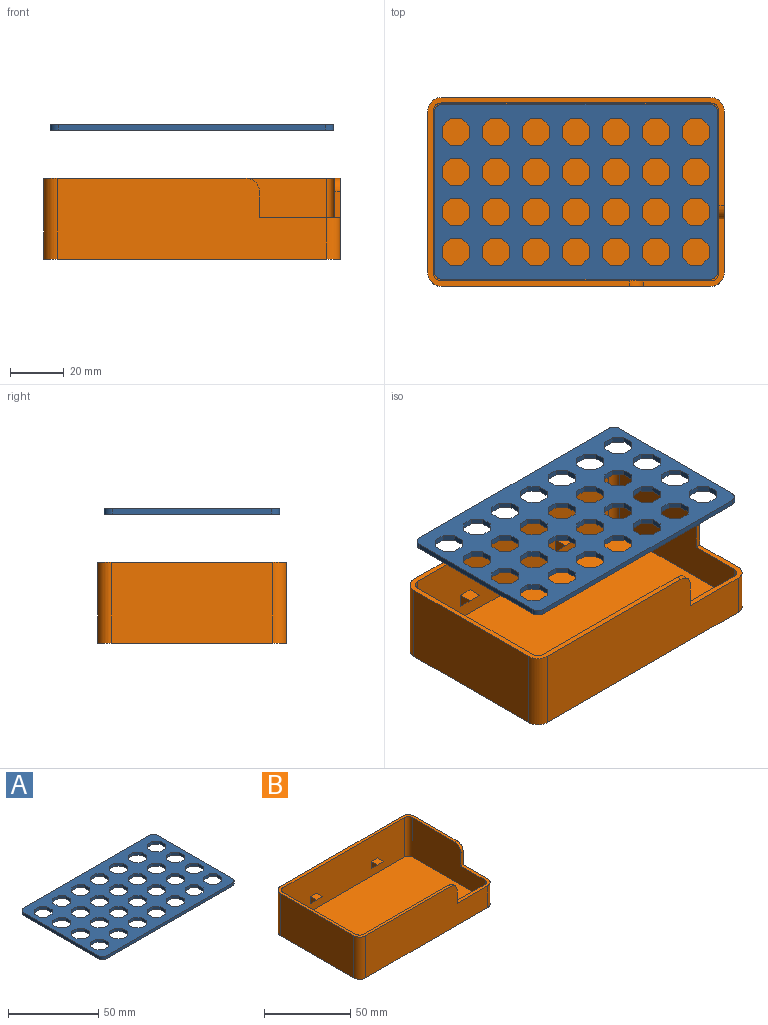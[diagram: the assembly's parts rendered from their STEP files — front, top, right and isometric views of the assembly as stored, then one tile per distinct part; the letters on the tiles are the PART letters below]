
ASSEMBLY  parts=2 mates=1
PART A: 234 faces, bbox 105x65x2 mm
  f0: plane 59x2mm, normal (1,0,0), area 118mm2, adj f1,f231,f232,f233
  f1: cylinder r=3mm len=3mm, axis (0,0,-1), area 9.4mm2, adj f0,f2,f232,f233
  f2: plane 99x2mm, normal (0,1,0), area 198mm2, adj f1,f3,f232,f233
  f3: cylinder r=3mm len=3mm, axis (0,0,-1), area 9.4mm2, adj f2,f4,f232,f233
  f4: plane 59x2mm, normal (-1,0,0), area 118mm2, adj f3,f5,f232,f233
  f5: cylinder r=3mm len=3mm, axis (0,0,-1), area 9.4mm2, adj f4,f6,f232,f233
  f6: plane 99x2mm, normal (0,-1,0), area 198mm2, adj f5,f231,f232,f233
  f7: plane 4.14x2mm, normal (0,-1,0), area 8.3mm2, adj f8,f203,f232,f233
  f8: plane 2.93x2.93mm, normal (-0.71,-0.71,0), area 8.3mm2, adj f7,f9,f232,f233
  f9: plane 4.14x2mm, normal (-1,0,0), area 8.3mm2, adj f8,f10,f232,f233
  f10: plane 2.93x2.93mm, normal (-0.71,0.71,0), area 8.3mm2, adj f9,f11,f232,f233
  f11: plane 4.14x2mm, normal (0,1,0), area 8.3mm2, adj f10,f12,f232,f233
  f12: plane 2.93x2.93mm, normal (0.71,0.71,0), area 8.3mm2, adj f11,f13,f232,f233
  f13: plane 4.14x2mm, normal (1,0,0), area 8.3mm2, adj f12,f203,f232,f233
  f14: plane 4.14x2mm, normal (-1,0,0), area 8.3mm2, adj f15,f204,f232,f233
  f15: plane 2.93x2.93mm, normal (-0.71,0.71,0), area 8.3mm2, adj f14,f16,f232,f233
  f16: plane 4.14x2mm, normal (0,1,0), area 8.3mm2, adj f15,f17,f232,f233
  f17: plane 2.93x2.93mm, normal (0.71,0.71,0), area 8.3mm2, adj f16,f18,f232,f233
  f18: plane 4.14x2mm, normal (1,0,0), area 8.3mm2, adj f17,f19,f232,f233
  f19: plane 2.93x2.93mm, normal (0.71,-0.71,0), area 8.3mm2, adj f18,f20,f232,f233
  f20: plane 4.14x2mm, normal (0,-1,0), area 8.3mm2, adj f19,f204,f232,f233
  f21: plane 4.14x2mm, normal (-1,0,0), area 8.3mm2, adj f22,f205,f232,f233
  f22: plane 2.93x2.93mm, normal (-0.71,0.71,0), area 8.3mm2, adj f21,f23,f232,f233
  f23: plane 4.14x2mm, normal (0,1,0), area 8.3mm2, adj f22,f24,f232,f233
  f24: plane 2.93x2.93mm, normal (0.71,0.71,0), area 8.3mm2, adj f23,f25,f232,f233
  f25: plane 4.14x2mm, normal (1,0,0), area 8.3mm2, adj f24,f26,f232,f233
  f26: plane 2.93x2.93mm, normal (0.71,-0.71,0), area 8.3mm2, adj f25,f27,f232,f233
  f27: plane 4.14x2mm, normal (0,-1,0), area 8.3mm2, adj f26,f205,f232,f233
  f28: plane 4.14x2mm, normal (-1,0,0), area 8.3mm2, adj f29,f206,f232,f233
  f29: plane 2.93x2.93mm, normal (-0.71,0.71,0), area 8.3mm2, adj f28,f30,f232,f233
  f30: plane 4.14x2mm, normal (0,1,0), area 8.3mm2, adj f29,f31,f232,f233
  f31: plane 2.93x2.93mm, normal (0.71,0.71,0), area 8.3mm2, adj f30,f32,f232,f233
  f32: plane 4.14x2mm, normal (1,0,0), area 8.3mm2, adj f31,f33,f232,f233
  f33: plane 2.93x2.93mm, normal (0.71,-0.71,0), area 8.3mm2, adj f32,f34,f232,f233
  f34: plane 4.14x2mm, normal (0,-1,0), area 8.3mm2, adj f33,f206,f232,f233
  f35: plane 4.14x2mm, normal (-1,0,0), area 8.3mm2, adj f36,f207,f232,f233
  f36: plane 2.93x2.93mm, normal (-0.71,0.71,0), area 8.3mm2, adj f35,f37,f232,f233
  f37: plane 4.14x2mm, normal (0,1,0), area 8.3mm2, adj f36,f38,f232,f233
  f38: plane 2.93x2.93mm, normal (0.71,0.71,0), area 8.3mm2, adj f37,f39,f232,f233
  f39: plane 4.14x2mm, normal (1,0,0), area 8.3mm2, adj f38,f40,f232,f233
  f40: plane 2.93x2.93mm, normal (0.71,-0.71,0), area 8.3mm2, adj f39,f41,f232,f233
  f41: plane 4.14x2mm, normal (0,-1,0), area 8.3mm2, adj f40,f207,f232,f233
  f42: plane 4.14x2mm, normal (-1,0,0), area 8.3mm2, adj f43,f208,f232,f233
  f43: plane 2.93x2.93mm, normal (-0.71,0.71,0), area 8.3mm2, adj f42,f44,f232,f233
  f44: plane 4.14x2mm, normal (0,1,0), area 8.3mm2, adj f43,f45,f232,f233
  f45: plane 2.93x2.93mm, normal (0.71,0.71,0), area 8.3mm2, adj f44,f46,f232,f233
  f46: plane 4.14x2mm, normal (1,0,0), area 8.3mm2, adj f45,f47,f232,f233
  f47: plane 2.93x2.93mm, normal (0.71,-0.71,0), area 8.3mm2, adj f46,f48,f232,f233
  f48: plane 4.14x2mm, normal (0,-1,0), area 8.3mm2, adj f47,f208,f232,f233
  f49: plane 4.14x2mm, normal (-1,0,0), area 8.3mm2, adj f50,f209,f232,f233
  f50: plane 2.93x2.93mm, normal (-0.71,0.71,0), area 8.3mm2, adj f49,f51,f232,f233
  f51: plane 4.14x2mm, normal (0,1,0), area 8.3mm2, adj f50,f52,f232,f233
  f52: plane 2.93x2.93mm, normal (0.71,0.71,0), area 8.3mm2, adj f51,f53,f232,f233
  f53: plane 4.14x2mm, normal (1,0,0), area 8.3mm2, adj f52,f54,f232,f233
  f54: plane 2.93x2.93mm, normal (0.71,-0.71,0), area 8.3mm2, adj f53,f55,f232,f233
  f55: plane 4.14x2mm, normal (0,-1,0), area 8.3mm2, adj f54,f209,f232,f233
  f56: plane 4.14x2mm, normal (-1,0,0), area 8.3mm2, adj f57,f210,f232,f233
  f57: plane 2.93x2.93mm, normal (-0.71,0.71,0), area 8.3mm2, adj f56,f58,f232,f233
  f58: plane 4.14x2mm, normal (0,1,0), area 8.3mm2, adj f57,f59,f232,f233
  f59: plane 2.93x2.93mm, normal (0.71,0.71,0), area 8.3mm2, adj f58,f60,f232,f233
  f60: plane 4.14x2mm, normal (1,0,0), area 8.3mm2, adj f59,f61,f232,f233
  f61: plane 2.93x2.93mm, normal (0.71,-0.71,0), area 8.3mm2, adj f60,f62,f232,f233
  f62: plane 4.14x2mm, normal (0,-1,0), area 8.3mm2, adj f61,f210,f232,f233
  f63: plane 4.14x2mm, normal (-1,0,0), area 8.3mm2, adj f64,f211,f232,f233
  f64: plane 2.93x2.93mm, normal (-0.71,0.71,0), area 8.3mm2, adj f63,f65,f232,f233
  f65: plane 4.14x2mm, normal (0,1,0), area 8.3mm2, adj f64,f66,f232,f233
  f66: plane 2.93x2.93mm, normal (0.71,0.71,0), area 8.3mm2, adj f65,f67,f232,f233
  f67: plane 4.14x2mm, normal (1,0,0), area 8.3mm2, adj f66,f68,f232,f233
  f68: plane 2.93x2.93mm, normal (0.71,-0.71,0), area 8.3mm2, adj f67,f69,f232,f233
  f69: plane 4.14x2mm, normal (0,-1,0), area 8.3mm2, adj f68,f211,f232,f233
  f70: plane 4.14x2mm, normal (-1,0,0), area 8.3mm2, adj f71,f212,f232,f233
  f71: plane 2.93x2.93mm, normal (-0.71,0.71,0), area 8.3mm2, adj f70,f72,f232,f233
  f72: plane 4.14x2mm, normal (0,1,0), area 8.3mm2, adj f71,f73,f232,f233
  f73: plane 2.93x2.93mm, normal (0.71,0.71,0), area 8.3mm2, adj f72,f74,f232,f233
  f74: plane 4.14x2mm, normal (1,0,0), area 8.3mm2, adj f73,f75,f232,f233
  f75: plane 2.93x2.93mm, normal (0.71,-0.71,0), area 8.3mm2, adj f74,f76,f232,f233
  f76: plane 4.14x2mm, normal (0,-1,0), area 8.3mm2, adj f75,f212,f232,f233
  f77: plane 4.14x2mm, normal (-1,0,0), area 8.3mm2, adj f78,f213,f232,f233
  f78: plane 2.93x2.93mm, normal (-0.71,0.71,0), area 8.3mm2, adj f77,f79,f232,f233
  f79: plane 4.14x2mm, normal (0,1,0), area 8.3mm2, adj f78,f80,f232,f233
  f80: plane 2.93x2.93mm, normal (0.71,0.71,0), area 8.3mm2, adj f79,f81,f232,f233
  f81: plane 4.14x2mm, normal (1,0,0), area 8.3mm2, adj f80,f82,f232,f233
  f82: plane 2.93x2.93mm, normal (0.71,-0.71,0), area 8.3mm2, adj f81,f83,f232,f233
  f83: plane 4.14x2mm, normal (0,-1,0), area 8.3mm2, adj f82,f213,f232,f233
  f84: plane 4.14x2mm, normal (-1,0,0), area 8.3mm2, adj f85,f214,f232,f233
  f85: plane 2.93x2.93mm, normal (-0.71,0.71,0), area 8.3mm2, adj f84,f86,f232,f233
  f86: plane 4.14x2mm, normal (0,1,0), area 8.3mm2, adj f85,f87,f232,f233
  f87: plane 2.93x2.93mm, normal (0.71,0.71,0), area 8.3mm2, adj f86,f88,f232,f233
  f88: plane 4.14x2mm, normal (1,0,0), area 8.3mm2, adj f87,f89,f232,f233
  f89: plane 2.93x2.93mm, normal (0.71,-0.71,0), area 8.3mm2, adj f88,f90,f232,f233
  f90: plane 4.14x2mm, normal (0,-1,0), area 8.3mm2, adj f89,f214,f232,f233
  f91: plane 4.14x2mm, normal (-1,0,0), area 8.3mm2, adj f92,f215,f232,f233
  f92: plane 2.93x2.93mm, normal (-0.71,0.71,0), area 8.3mm2, adj f91,f93,f232,f233
  f93: plane 4.14x2mm, normal (0,1,0), area 8.3mm2, adj f92,f94,f232,f233
  f94: plane 2.93x2.93mm, normal (0.71,0.71,0), area 8.3mm2, adj f93,f95,f232,f233
  f95: plane 4.14x2mm, normal (1,0,0), area 8.3mm2, adj f94,f96,f232,f233
  f96: plane 2.93x2.93mm, normal (0.71,-0.71,0), area 8.3mm2, adj f95,f97,f232,f233
  f97: plane 4.14x2mm, normal (0,-1,0), area 8.3mm2, adj f96,f215,f232,f233
  f98: plane 4.14x2mm, normal (-1,0,0), area 8.3mm2, adj f99,f216,f232,f233
  f99: plane 2.93x2.93mm, normal (-0.71,0.71,0), area 8.3mm2, adj f98,f100,f232,f233
  f100: plane 4.14x2mm, normal (0,1,0), area 8.3mm2, adj f99,f101,f232,f233
  f101: plane 2.93x2.93mm, normal (0.71,0.71,0), area 8.3mm2, adj f100,f102,f232,f233
  f102: plane 4.14x2mm, normal (1,0,0), area 8.3mm2, adj f101,f103,f232,f233
  f103: plane 2.93x2.93mm, normal (0.71,-0.71,0), area 8.3mm2, adj f102,f104,f232,f233
  f104: plane 4.14x2mm, normal (0,-1,0), area 8.3mm2, adj f103,f216,f232,f233
  f105: plane 4.14x2mm, normal (-1,0,0), area 8.3mm2, adj f106,f217,f232,f233
  f106: plane 2.93x2.93mm, normal (-0.71,0.71,0), area 8.3mm2, adj f105,f107,f232,f233
  f107: plane 4.14x2mm, normal (0,1,0), area 8.3mm2, adj f106,f108,f232,f233
  f108: plane 2.93x2.93mm, normal (0.71,0.71,0), area 8.3mm2, adj f107,f109,f232,f233
  f109: plane 4.14x2mm, normal (1,0,0), area 8.3mm2, adj f108,f110,f232,f233
  f110: plane 2.93x2.93mm, normal (0.71,-0.71,0), area 8.3mm2, adj f109,f111,f232,f233
  f111: plane 4.14x2mm, normal (0,-1,0), area 8.3mm2, adj f110,f217,f232,f233
  f112: plane 4.14x2mm, normal (-1,0,0), area 8.3mm2, adj f113,f218,f232,f233
  f113: plane 2.93x2.93mm, normal (-0.71,0.71,0), area 8.3mm2, adj f112,f114,f232,f233
  f114: plane 4.14x2mm, normal (0,1,0), area 8.3mm2, adj f113,f115,f232,f233
  f115: plane 2.93x2.93mm, normal (0.71,0.71,0), area 8.3mm2, adj f114,f116,f232,f233
  f116: plane 4.14x2mm, normal (1,0,0), area 8.3mm2, adj f115,f117,f232,f233
  f117: plane 2.93x2.93mm, normal (0.71,-0.71,0), area 8.3mm2, adj f116,f118,f232,f233
  f118: plane 4.14x2mm, normal (0,-1,0), area 8.3mm2, adj f117,f218,f232,f233
  f119: plane 4.14x2mm, normal (-1,0,0), area 8.3mm2, adj f120,f219,f232,f233
  f120: plane 2.93x2.93mm, normal (-0.71,0.71,0), area 8.3mm2, adj f119,f121,f232,f233
  f121: plane 4.14x2mm, normal (0,1,0), area 8.3mm2, adj f120,f122,f232,f233
  f122: plane 2.93x2.93mm, normal (0.71,0.71,0), area 8.3mm2, adj f121,f123,f232,f233
  f123: plane 4.14x2mm, normal (1,0,0), area 8.3mm2, adj f122,f124,f232,f233
  f124: plane 2.93x2.93mm, normal (0.71,-0.71,0), area 8.3mm2, adj f123,f125,f232,f233
  f125: plane 4.14x2mm, normal (0,-1,0), area 8.3mm2, adj f124,f219,f232,f233
  f126: plane 4.14x2mm, normal (-1,0,0), area 8.3mm2, adj f127,f220,f232,f233
  f127: plane 2.93x2.93mm, normal (-0.71,0.71,0), area 8.3mm2, adj f126,f128,f232,f233
  f128: plane 4.14x2mm, normal (0,1,0), area 8.3mm2, adj f127,f129,f232,f233
  f129: plane 2.93x2.93mm, normal (0.71,0.71,0), area 8.3mm2, adj f128,f130,f232,f233
  f130: plane 4.14x2mm, normal (1,0,0), area 8.3mm2, adj f129,f131,f232,f233
  f131: plane 2.93x2.93mm, normal (0.71,-0.71,0), area 8.3mm2, adj f130,f132,f232,f233
  f132: plane 4.14x2mm, normal (0,-1,0), area 8.3mm2, adj f131,f220,f232,f233
  f133: plane 4.14x2mm, normal (-1,0,0), area 8.3mm2, adj f134,f221,f232,f233
  f134: plane 2.93x2.93mm, normal (-0.71,0.71,0), area 8.3mm2, adj f133,f135,f232,f233
  f135: plane 4.14x2mm, normal (0,1,0), area 8.3mm2, adj f134,f136,f232,f233
  f136: plane 2.93x2.93mm, normal (0.71,0.71,0), area 8.3mm2, adj f135,f137,f232,f233
  f137: plane 4.14x2mm, normal (1,0,0), area 8.3mm2, adj f136,f138,f232,f233
  f138: plane 2.93x2.93mm, normal (0.71,-0.71,0), area 8.3mm2, adj f137,f139,f232,f233
  f139: plane 4.14x2mm, normal (0,-1,0), area 8.3mm2, adj f138,f221,f232,f233
  f140: plane 4.14x2mm, normal (-1,0,0), area 8.3mm2, adj f141,f222,f232,f233
  f141: plane 2.93x2.93mm, normal (-0.71,0.71,0), area 8.3mm2, adj f140,f142,f232,f233
  f142: plane 4.14x2mm, normal (0,1,0), area 8.3mm2, adj f141,f143,f232,f233
  f143: plane 2.93x2.93mm, normal (0.71,0.71,0), area 8.3mm2, adj f142,f144,f232,f233
  f144: plane 4.14x2mm, normal (1,0,0), area 8.3mm2, adj f143,f145,f232,f233
  f145: plane 2.93x2.93mm, normal (0.71,-0.71,0), area 8.3mm2, adj f144,f146,f232,f233
  f146: plane 4.14x2mm, normal (0,-1,0), area 8.3mm2, adj f145,f222,f232,f233
  f147: plane 4.14x2mm, normal (-1,0,0), area 8.3mm2, adj f148,f223,f232,f233
  f148: plane 2.93x2.93mm, normal (-0.71,0.71,0), area 8.3mm2, adj f147,f149,f232,f233
  f149: plane 4.14x2mm, normal (0,1,0), area 8.3mm2, adj f148,f150,f232,f233
  f150: plane 2.93x2.93mm, normal (0.71,0.71,0), area 8.3mm2, adj f149,f151,f232,f233
  f151: plane 4.14x2mm, normal (1,0,0), area 8.3mm2, adj f150,f152,f232,f233
  f152: plane 2.93x2.93mm, normal (0.71,-0.71,0), area 8.3mm2, adj f151,f153,f232,f233
  f153: plane 4.14x2mm, normal (0,-1,0), area 8.3mm2, adj f152,f223,f232,f233
  f154: plane 4.14x2mm, normal (-1,0,0), area 8.3mm2, adj f155,f224,f232,f233
  f155: plane 2.93x2.93mm, normal (-0.71,0.71,0), area 8.3mm2, adj f154,f156,f232,f233
  f156: plane 4.14x2mm, normal (0,1,0), area 8.3mm2, adj f155,f157,f232,f233
  f157: plane 2.93x2.93mm, normal (0.71,0.71,0), area 8.3mm2, adj f156,f158,f232,f233
  f158: plane 4.14x2mm, normal (1,0,0), area 8.3mm2, adj f157,f159,f232,f233
  f159: plane 2.93x2.93mm, normal (0.71,-0.71,0), area 8.3mm2, adj f158,f160,f232,f233
  f160: plane 4.14x2mm, normal (0,-1,0), area 8.3mm2, adj f159,f224,f232,f233
  f161: plane 4.14x2mm, normal (-1,0,0), area 8.3mm2, adj f162,f225,f232,f233
  f162: plane 2.93x2.93mm, normal (-0.71,0.71,0), area 8.3mm2, adj f161,f163,f232,f233
  f163: plane 4.14x2mm, normal (0,1,0), area 8.3mm2, adj f162,f164,f232,f233
  f164: plane 2.93x2.93mm, normal (0.71,0.71,0), area 8.3mm2, adj f163,f165,f232,f233
  f165: plane 4.14x2mm, normal (1,0,0), area 8.3mm2, adj f164,f166,f232,f233
  f166: plane 2.93x2.93mm, normal (0.71,-0.71,0), area 8.3mm2, adj f165,f167,f232,f233
  f167: plane 4.14x2mm, normal (0,-1,0), area 8.3mm2, adj f166,f225,f232,f233
  f168: plane 4.14x2mm, normal (-1,0,0), area 8.3mm2, adj f169,f226,f232,f233
  f169: plane 2.93x2.93mm, normal (-0.71,0.71,0), area 8.3mm2, adj f168,f170,f232,f233
  f170: plane 4.14x2mm, normal (0,1,0), area 8.3mm2, adj f169,f171,f232,f233
  f171: plane 2.93x2.93mm, normal (0.71,0.71,0), area 8.3mm2, adj f170,f172,f232,f233
  f172: plane 4.14x2mm, normal (1,0,0), area 8.3mm2, adj f171,f173,f232,f233
  f173: plane 2.93x2.93mm, normal (0.71,-0.71,0), area 8.3mm2, adj f172,f174,f232,f233
  f174: plane 4.14x2mm, normal (0,-1,0), area 8.3mm2, adj f173,f226,f232,f233
  f175: plane 4.14x2mm, normal (-1,0,0), area 8.3mm2, adj f176,f227,f232,f233
  f176: plane 2.93x2.93mm, normal (-0.71,0.71,0), area 8.3mm2, adj f175,f177,f232,f233
  f177: plane 4.14x2mm, normal (0,1,0), area 8.3mm2, adj f176,f178,f232,f233
  f178: plane 2.93x2.93mm, normal (0.71,0.71,0), area 8.3mm2, adj f177,f179,f232,f233
  f179: plane 4.14x2mm, normal (1,0,0), area 8.3mm2, adj f178,f180,f232,f233
  f180: plane 2.93x2.93mm, normal (0.71,-0.71,0), area 8.3mm2, adj f179,f181,f232,f233
  f181: plane 4.14x2mm, normal (0,-1,0), area 8.3mm2, adj f180,f227,f232,f233
  f182: plane 4.14x2mm, normal (-1,0,0), area 8.3mm2, adj f183,f228,f232,f233
  f183: plane 2.93x2.93mm, normal (-0.71,0.71,0), area 8.3mm2, adj f182,f184,f232,f233
  f184: plane 4.14x2mm, normal (0,1,0), area 8.3mm2, adj f183,f185,f232,f233
  f185: plane 2.93x2.93mm, normal (0.71,0.71,0), area 8.3mm2, adj f184,f186,f232,f233
  f186: plane 4.14x2mm, normal (1,0,0), area 8.3mm2, adj f185,f187,f232,f233
  f187: plane 2.93x2.93mm, normal (0.71,-0.71,0), area 8.3mm2, adj f186,f188,f232,f233
  f188: plane 4.14x2mm, normal (0,-1,0), area 8.3mm2, adj f187,f228,f232,f233
  f189: plane 4.14x2mm, normal (-1,0,0), area 8.3mm2, adj f190,f229,f232,f233
  f190: plane 2.93x2.93mm, normal (-0.71,0.71,0), area 8.3mm2, adj f189,f191,f232,f233
  f191: plane 4.14x2mm, normal (0,1,0), area 8.3mm2, adj f190,f192,f232,f233
  f192: plane 2.93x2.93mm, normal (0.71,0.71,0), area 8.3mm2, adj f191,f193,f232,f233
  f193: plane 4.14x2mm, normal (1,0,0), area 8.3mm2, adj f192,f194,f232,f233
  f194: plane 2.93x2.93mm, normal (0.71,-0.71,0), area 8.3mm2, adj f193,f195,f232,f233
  f195: plane 4.14x2mm, normal (0,-1,0), area 8.3mm2, adj f194,f229,f232,f233
  f196: plane 4.14x2mm, normal (-1,0,0), area 8.3mm2, adj f197,f230,f232,f233
  f197: plane 2.93x2.93mm, normal (-0.71,0.71,0), area 8.3mm2, adj f196,f198,f232,f233
  f198: plane 4.14x2mm, normal (0,1,0), area 8.3mm2, adj f197,f199,f232,f233
  f199: plane 2.93x2.93mm, normal (0.71,0.71,0), area 8.3mm2, adj f198,f200,f232,f233
  f200: plane 4.14x2mm, normal (1,0,0), area 8.3mm2, adj f199,f201,f232,f233
  f201: plane 2.93x2.93mm, normal (0.71,-0.71,0), area 8.3mm2, adj f200,f202,f232,f233
  f202: plane 4.14x2mm, normal (0,-1,0), area 8.3mm2, adj f201,f230,f232,f233
  f203: plane 2.93x2.93mm, normal (0.71,-0.71,0), area 8.3mm2, adj f7,f13,f232,f233
  f204: plane 2.93x2.93mm, normal (-0.71,-0.71,0), area 8.3mm2, adj f14,f20,f232,f233
  f205: plane 2.93x2.93mm, normal (-0.71,-0.71,0), area 8.3mm2, adj f21,f27,f232,f233
  f206: plane 2.93x2.93mm, normal (-0.71,-0.71,0), area 8.3mm2, adj f28,f34,f232,f233
  f207: plane 2.93x2.93mm, normal (-0.71,-0.71,0), area 8.3mm2, adj f35,f41,f232,f233
  f208: plane 2.93x2.93mm, normal (-0.71,-0.71,0), area 8.3mm2, adj f42,f48,f232,f233
  f209: plane 2.93x2.93mm, normal (-0.71,-0.71,0), area 8.3mm2, adj f49,f55,f232,f233
  f210: plane 2.93x2.93mm, normal (-0.71,-0.71,0), area 8.3mm2, adj f56,f62,f232,f233
  f211: plane 2.93x2.93mm, normal (-0.71,-0.71,0), area 8.3mm2, adj f63,f69,f232,f233
  f212: plane 2.93x2.93mm, normal (-0.71,-0.71,0), area 8.3mm2, adj f70,f76,f232,f233
  f213: plane 2.93x2.93mm, normal (-0.71,-0.71,0), area 8.3mm2, adj f77,f83,f232,f233
  f214: plane 2.93x2.93mm, normal (-0.71,-0.71,0), area 8.3mm2, adj f84,f90,f232,f233
  f215: plane 2.93x2.93mm, normal (-0.71,-0.71,0), area 8.3mm2, adj f91,f97,f232,f233
  f216: plane 2.93x2.93mm, normal (-0.71,-0.71,0), area 8.3mm2, adj f98,f104,f232,f233
  f217: plane 2.93x2.93mm, normal (-0.71,-0.71,0), area 8.3mm2, adj f105,f111,f232,f233
  f218: plane 2.93x2.93mm, normal (-0.71,-0.71,0), area 8.3mm2, adj f112,f118,f232,f233
  f219: plane 2.93x2.93mm, normal (-0.71,-0.71,0), area 8.3mm2, adj f119,f125,f232,f233
  f220: plane 2.93x2.93mm, normal (-0.71,-0.71,0), area 8.3mm2, adj f126,f132,f232,f233
  f221: plane 2.93x2.93mm, normal (-0.71,-0.71,0), area 8.3mm2, adj f133,f139,f232,f233
  f222: plane 2.93x2.93mm, normal (-0.71,-0.71,0), area 8.3mm2, adj f140,f146,f232,f233
  f223: plane 2.93x2.93mm, normal (-0.71,-0.71,0), area 8.3mm2, adj f147,f153,f232,f233
  f224: plane 2.93x2.93mm, normal (-0.71,-0.71,0), area 8.3mm2, adj f154,f160,f232,f233
  f225: plane 2.93x2.93mm, normal (-0.71,-0.71,0), area 8.3mm2, adj f161,f167,f232,f233
  f226: plane 2.93x2.93mm, normal (-0.71,-0.71,0), area 8.3mm2, adj f168,f174,f232,f233
  f227: plane 2.93x2.93mm, normal (-0.71,-0.71,0), area 8.3mm2, adj f175,f181,f232,f233
  f228: plane 2.93x2.93mm, normal (-0.71,-0.71,0), area 8.3mm2, adj f182,f188,f232,f233
  f229: plane 2.93x2.93mm, normal (-0.71,-0.71,0), area 8.3mm2, adj f189,f195,f232,f233
  f230: plane 2.93x2.93mm, normal (-0.71,-0.71,0), area 8.3mm2, adj f196,f202,f232,f233
  f231: cylinder r=3mm len=3mm, axis (0,0,-1), area 9.4mm2, adj f0,f6,f232,f233
  f232: plane 105x65mm, normal (0,0,1), area 4497.7mm2, adj f0,f1,f2,f3,f4,f5,f6,f7
  f233: plane 105x65mm, normal (0,0,-1), area 4497.7mm2, adj f0,f1,f2,f3,f4,f5,f6,f7
PART B: 40 faces, bbox 110x70x30 mm
  f0: plane 110x70mm, normal (0,0,1), area 567.7mm2, adj f2,f3,f4,f5,f7,f8,f9,f10
  f1: cylinder r=3mm len=13.5mm, axis (0,0,-1), area 63.6mm2, adj f3,f11,f18,f36
  f2: plane 100x30mm, normal (0,-1,0), area 2632.1mm2, adj f0,f5,f6,f17,f35,f36,f37
  f3: plane 100x28mm, normal (0,1,0), area 2382.1mm2, adj f0,f1,f12,f18,f27,f28,f29,f30
  f4: plane 60x30mm, normal (-1,0,0), area 1800mm2, adj f0,f5,f16,f17
  f5: cylinder r=5mm len=30mm, axis (0,0,-1), area 235.6mm2, adj f0,f2,f4,f17
  f6: cylinder r=5mm len=15.5mm, axis (0,0,-1), area 121.7mm2, adj f2,f7,f17,f36
  f7: plane 60x30mm, normal (1,0,0), area 1504.6mm2, adj f0,f6,f8,f17,f36,f38,f39
  f8: cylinder r=5mm len=30mm, axis (0,0,-1), area 235.6mm2, adj f0,f7,f9,f17
  f9: plane 100x30mm, normal (0,1,0), area 3000mm2, adj f0,f8,f16,f17
  f10: cylinder r=3mm len=28mm, axis (0,0,-1), area 131.9mm2, adj f0,f11,f15,f18
  f11: plane 60x28mm, normal (-1,0,0), area 1384.6mm2, adj f0,f1,f10,f18,f36,f38,f39
  f12: cylinder r=3mm len=28mm, axis (0,0,-1), area 131.9mm2, adj f0,f3,f13,f18
  f13: plane 60x28mm, normal (1,0,0), area 1680mm2, adj f0,f12,f14,f18
  f14: cylinder r=3mm len=28mm, axis (0,0,-1), area 131.9mm2, adj f0,f13,f15,f18
  f15: plane 100x28mm, normal (0,-1,0), area 2750mm2, adj f0,f10,f14,f18,f19,f20,f21,f22
  f16: cylinder r=5mm len=30mm, axis (0,0,-1), area 235.6mm2, adj f0,f4,f9,f17
  f17: plane 110x70mm, normal (0,0,-1), area 7678.5mm2, adj f2,f4,f5,f6,f7,f8,f9,f16
  f18: plane 106x66mm, normal (0,0,1), area 6988.3mm2, adj f1,f3,f10,f11,f12,f13,f14,f15
  f19: plane 5x5mm, normal (-1,0,0), area 12.5mm2, adj f15,f21,f25
  f20: plane 5x5mm, normal (1,0,0), area 12.5mm2, adj f15,f21,f25
  f21: plane 5x5mm, normal (0,0,1), area 25mm2, adj f15,f19,f20,f25
  f22: plane 5x5mm, normal (-1,0,0), area 12.5mm2, adj f15,f24,f26
  f23: plane 5x5mm, normal (1,0,0), area 12.5mm2, adj f15,f24,f26
  f24: plane 5x5mm, normal (0,0,1), area 25mm2, adj f15,f22,f23,f26
  f25: plane 5x5mm, normal (0,-0.71,-0.71), area 35.4mm2, adj f15,f19,f20,f21
  f26: plane 5x5mm, normal (0,-0.71,-0.71), area 35.4mm2, adj f15,f22,f23,f24
  f27: plane 5x5mm, normal (1,0,0), area 12.5mm2, adj f3,f29,f34
  f28: plane 5x5mm, normal (-1,0,0), area 12.5mm2, adj f3,f29,f34
  f29: plane 5x5mm, normal (0,0,1), area 25mm2, adj f3,f27,f28,f34
  f30: plane 5x5mm, normal (1,0,0), area 12.5mm2, adj f3,f32,f33
  f31: plane 5x5mm, normal (-1,0,0), area 12.5mm2, adj f3,f32,f33
  f32: plane 5x5mm, normal (0,0,1), area 25mm2, adj f3,f30,f31,f33
  f33: plane 5x5mm, normal (0,0.71,-0.71), area 35.4mm2, adj f3,f30,f31,f32
  f34: plane 5x5mm, normal (0,0.71,-0.71), area 35.4mm2, adj f3,f27,f28,f29
  f35: plane 9.5x2mm, normal (1,0,0), area 19mm2, adj f2,f3,f36,f37
  f36: plane 30x25mm, normal (0,0,1), area 102.6mm2, adj f1,f2,f3,f6,f7,f11,f35,f38
  f37: cylinder r=5mm len=5mm, axis (0,1,0), area 15.7mm2, adj f0,f2,f3,f35
  f38: plane 9.5x2mm, normal (0,-1,0), area 19mm2, adj f7,f11,f36,f39
  f39: cylinder r=5mm len=5mm, axis (1,0,0), area 15.7mm2, adj f0,f7,f11,f38
PLACE A rot(axis=(1,0,0),180deg) t=(-0.01,0,49.93)mm
PLACE B at identity fixed
MATE slider A.f233 <-> B.f18  axis (0,0,1) through (0,0,49.93)mm
